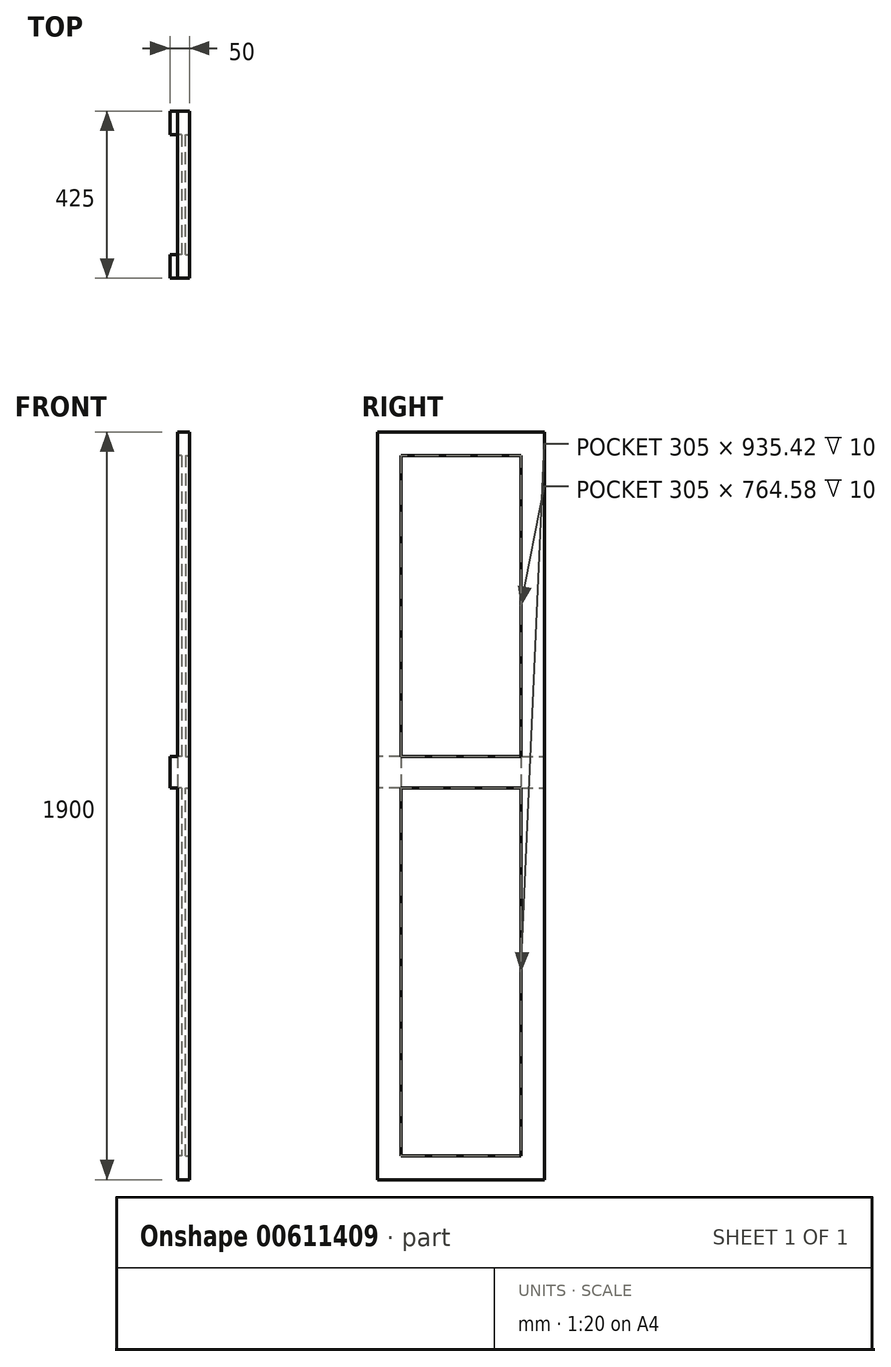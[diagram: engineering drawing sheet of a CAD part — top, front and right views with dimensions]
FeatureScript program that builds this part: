
annotation { "Feature Type Name" : "Feature", "Feature Type Description" : "" }
export const myFeature = defineFeature(function(context is Context, id is Id, definition is map)
    precondition{}
    {
        {
            var Q0;
            Q0=qCreatedBy(makeId("Right.planeOp"),FACE);
            var sketch = newSketch(context, id + "F0", { "sketchPlane" : qUnion([Q0])});
            skLineSegment(sketch, "E0.bottom", {"start": v(0, 0) * mm, "end": v(425, 0) * mm});
            skLineSegment(sketch, "E0.top", {"start": v(0, 1900) * mm, "end": v(425, 1900) * mm});
            skLineSegment(sketch, "E0.left", {"start": v(0, 0) * mm, "end": v(0, 1900) * mm});
            skLineSegment(sketch, "E0.right", {"start": v(425, 0) * mm, "end": v(425, 1900) * mm});
            skSolve(sketch);
        }
        {
            var Q0;
            Q0=makeQuery(id+"F0.imprint","IMPRINT",FACE,{"disambiguationData":[TD([[makeQuery(id+"F0.imprint","IMPRINT",EDGE,{"derivedFrom":sQuery(id+"F0.wireOp",EDGE,"E0.bottom")}),1.0]])]});
            extrude(context, id + "F1", {"entities" : qUnion([Q0]), "depth" : 30 * mm, "offsetDistance" : 25 * mm});
        }
        {
            var Q0;
            Q0=makeQuery(id+"F1.opExtrude","CAP_FACE",FACE,{"disambiguationData":[OSD([sQuery(id+"F0.wireOp",EDGE,"E0.bottom"),sQuery(id+"F0.wireOp",EDGE,"E0.top"),sQuery(id+"F0.wireOp",EDGE,"E0.left"),sQuery(id+"F0.wireOp",EDGE,"E0.right")])],"isStart":false});
            var sketch = newSketch(context, id + "F2", { "sketchPlane" : qUnion([Q0])});
            skLineSegment(sketch, "E1.bottom", {"start": v(60, 1840) * mm, "end": v(365, 1840) * mm});
            skLineSegment(sketch, "E1.top", {"start": v(60, 1075.42) * mm, "end": v(365, 1075.42) * mm});
            skLineSegment(sketch, "E1.left", {"start": v(60, 1840) * mm, "end": v(60, 1075.42) * mm});
            skLineSegment(sketch, "E1.right", {"start": v(365, 1840) * mm, "end": v(365, 1075.42) * mm});
            skLineSegment(sketch, "E2.bottom", {"start": v(60, 60) * mm, "end": v(365, 60) * mm});
            skLineSegment(sketch, "E2.top", {"start": v(60, 995.42) * mm, "end": v(365, 995.42) * mm});
            skLineSegment(sketch, "E2.left", {"start": v(60, 60) * mm, "end": v(60, 995.42) * mm});
            skLineSegment(sketch, "E2.right", {"start": v(365, 60) * mm, "end": v(365, 995.42) * mm});
            skSolve(sketch);
        }
        {
            var Q0;
            Q0=makeQuery(id+"F2.imprint","IMPRINT",FACE,{"disambiguationData":[TD([[makeQuery(id+"F2.imprint","IMPRINT",EDGE,{"derivedFrom":sQuery(id+"F2.wireOp",EDGE,"E1.bottom")}),-1.0]])]});
            var Q1;
            Q1=makeQuery(id+"F2.imprint","IMPRINT",FACE,{"disambiguationData":[TD([[makeQuery(id+"F2.imprint","IMPRINT",EDGE,{"derivedFrom":sQuery(id+"F2.wireOp",EDGE,"E2.bottom")}),1.0]])]});
            extrude(context, id + "F3", {"entities" : qUnion([Q0, Q1]), "operationType" : NewBodyOperationType.REMOVE, "oppositeDirection" : true, "depth" : 10 * mm, "offsetDistance" : 25 * mm});
        }
        {
            var Q0;
            Q0=makeQuery(id+"F1.opExtrude","CAP_FACE",FACE,{"disambiguationData":[OSD([sQuery(id+"F0.wireOp",EDGE,"E0.bottom"),sQuery(id+"F0.wireOp",EDGE,"E0.top"),sQuery(id+"F0.wireOp",EDGE,"E0.left"),sQuery(id+"F0.wireOp",EDGE,"E0.right")])],"isStart":true});
            var sketch = newSketch(context, id + "F4", { "sketchPlane" : qUnion([Q0])});
            skLineSegment(sketch, "E3.bottom", {"start": v(-60, 1840) * mm, "end": v(-365, 1840) * mm});
            skLineSegment(sketch, "E3.top", {"start": v(-60, 1075.42) * mm, "end": v(-365, 1075.42) * mm});
            skLineSegment(sketch, "E3.left", {"start": v(-365, 1840) * mm, "end": v(-365, 1075.42) * mm});
            skLineSegment(sketch, "E3.right", {"start": v(-60, 1840) * mm, "end": v(-60, 1075.42) * mm});
            skLineSegment(sketch, "E4.bottom", {"start": v(-365, 995.42) * mm, "end": v(-60, 995.42) * mm});
            skLineSegment(sketch, "E4.top", {"start": v(-365, 60) * mm, "end": v(-60, 60) * mm});
            skLineSegment(sketch, "E4.left", {"start": v(-365, 995.42) * mm, "end": v(-365, 60) * mm});
            skLineSegment(sketch, "E4.right", {"start": v(-60, 995.42) * mm, "end": v(-60, 60) * mm});
            skSolve(sketch);
        }
        {
            var Q0;
            Q0 = qSketchRegion(id + "F4", true);
            extrude(context, id + "F5", {"entities" : qUnion([Q0]), "operationType" : NewBodyOperationType.REMOVE, "oppositeDirection" : true, "depth" : 10 * mm, "offsetDistance" : 25 * mm});
        }
        {
            var Q0;
            Q0=makeQuery(id+"F1.opExtrude","CAP_FACE",FACE,{"disambiguationData":[OSD([sQuery(id+"F0.wireOp",EDGE,"E0.bottom"),sQuery(id+"F0.wireOp",EDGE,"E0.top"),sQuery(id+"F0.wireOp",EDGE,"E0.left"),sQuery(id+"F0.wireOp",EDGE,"E0.right")])],"isStart":true});
            var sketch = newSketch(context, id + "F6", { "sketchPlane" : qUnion([Q0])});
            skLineSegment(sketch, "E5.bottom", {"start": v(-365, 1075.42) * mm, "end": v(-425, 1075.42) * mm});
            skLineSegment(sketch, "E5.top", {"start": v(-365, 995.42) * mm, "end": v(-425, 995.42) * mm});
            skLineSegment(sketch, "E5.left", {"start": v(-365, 1075.42) * mm, "end": v(-365, 995.42) * mm});
            skLineSegment(sketch, "E5.right", {"start": v(-425, 1075.42) * mm, "end": v(-425, 995.42) * mm});
            skLineSegment(sketch, "E6.bottom", {"start": v(-60, 1075.42) * mm, "end": v(0, 1075.42) * mm});
            skLineSegment(sketch, "E6.top", {"start": v(-60, 995.42) * mm, "end": v(0, 995.42) * mm});
            skLineSegment(sketch, "E6.left", {"start": v(-60, 1075.42) * mm, "end": v(-60, 995.42) * mm});
            skLineSegment(sketch, "E6.right", {"start": v(0, 1075.42) * mm, "end": v(0, 995.42) * mm});
            skSolve(sketch);
        }
        {
            var Q0;
            Q0=makeQuery(id+"F6.imprint","IMPRINT",FACE,{"disambiguationData":[TD([[makeQuery(id+"F6.imprint","IMPRINT",EDGE,{"derivedFrom":sQuery(id+"F6.wireOp",EDGE,"E5.bottom")}),1.0]])]});
            var Q1;
            Q1=makeQuery(id+"F6.imprint","IMPRINT",FACE,{"disambiguationData":[TD([[makeQuery(id+"F6.imprint","IMPRINT",EDGE,{"derivedFrom":sQuery(id+"F6.wireOp",EDGE,"E6.bottom")}),-1.0]])]});
            extrude(context, id + "F7", {"entities" : qUnion([Q0, Q1]), "operationType" : NewBodyOperationType.ADD, "depth" : 20 * mm, "offsetDistance" : 25 * mm});
        }
    });
